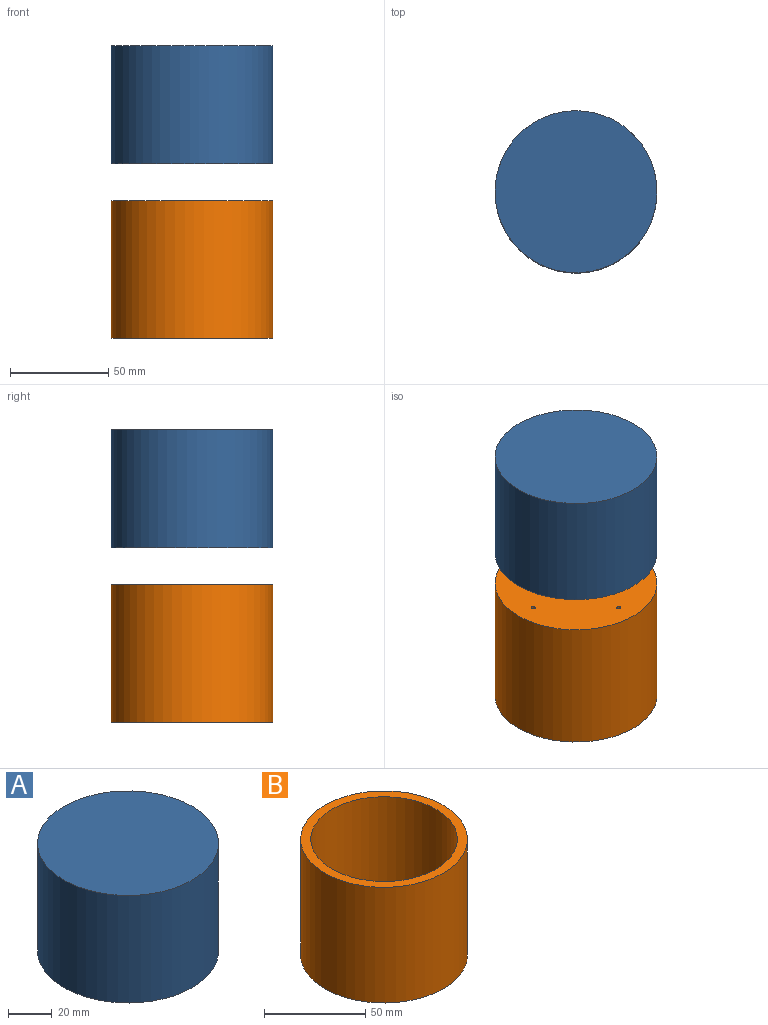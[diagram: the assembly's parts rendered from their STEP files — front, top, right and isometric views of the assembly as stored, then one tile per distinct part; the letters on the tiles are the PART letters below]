
ASSEMBLY  parts=2 mates=1
PART A: 33 faces, bbox 82.8x82.8x60.3 mm
  f0: cylinder r=36.25mm len=72.5mm, axis (0,0,1), area 11724.5mm2, adj f3,f4,f6,f8,f10,f12,f14,f17
  f1: cylinder r=41.25mm len=82.5mm, axis (0,0,-1), area 15550.9mm2, adj f2,f3
  f2: plane 82.5x82.5mm, normal (0,0,1), area 5345.6mm2, adj f1
  f3: plane 82.5x82.5mm, normal (0,0,-1), area 1614mm2, adj f0,f1,f4,f5,f6,f8,f9,f10
  f4: plane 20.26x10.26mm, normal (1,0,0), area 150.6mm2, adj f0,f3,f5,f22
  f5: plane 10.14x10.01mm, normal (0,-1,0), area 100.1mm2, adj f3,f4,f6,f7,f22
  f6: plane 20.26x10.26mm, normal (-1,0,0), area 150.6mm2, adj f0,f3,f5,f22
  f7: plane 8.5x0.35mm, normal (0,0,1), area 2mm2, adj f5,f22
  f8: plane 20.26x10.26mm, normal (0,-1,0), area 150.6mm2, adj f0,f3,f9,f23
  f9: plane 10.14x10.01mm, normal (-1,0,0), area 100.1mm2, adj f3,f8,f10,f11,f23
  f10: plane 20.26x10.26mm, normal (0,1,0), area 150.6mm2, adj f0,f3,f9,f23
  f11: plane 8.5x0.35mm, normal (0,0,1), area 2mm2, adj f9,f23
  f12: plane 20.26x10.26mm, normal (-1,0,0), area 150.6mm2, adj f0,f3,f13,f20
  f13: plane 10.14x10.01mm, normal (0,1,0), area 100.1mm2, adj f3,f12,f14,f15,f20
  f14: plane 20.26x10.26mm, normal (1,0,0), area 150.6mm2, adj f0,f3,f13,f20
  f15: plane 8.5x0.35mm, normal (0,0,1), area 2mm2, adj f13,f20
  f16: plane 10.14x10.01mm, normal (1,0,0), area 100.1mm2, adj f3,f17,f18,f19,f21
  f17: plane 20.26x10.26mm, normal (0,-1,0), area 150.6mm2, adj f0,f3,f16,f21
  f18: plane 20.26x10.26mm, normal (0,1,0), area 150.6mm2, adj f0,f3,f16,f21
  f19: plane 8.5x0.35mm, normal (0,0,1), area 2mm2, adj f16,f21
  f20: cone r=36.25mm half-angle=45deg, axis (0,0,1), area 144.3mm2, adj f0,f12,f13,f14,f15
  f21: cone r=36.25mm half-angle=45deg, axis (0,0,1), area 144.3mm2, adj f0,f16,f17,f18,f19
  f22: cone r=36.25mm half-angle=45deg, axis (0,0,1), area 144.3mm2, adj f0,f4,f5,f6,f7
  f23: cone r=36.25mm half-angle=45deg, axis (0,0,1), area 144.3mm2, adj f0,f8,f9,f10,f11
  f24: cylinder r=1mm len=8mm, axis (0,0,-1), area 50.3mm2, adj f3,f25
  f25: plane 2x2mm, normal (0,0,-1), area 3.1mm2, adj f24
  f26: cylinder r=1mm len=8mm, axis (0,0,-1), area 50.3mm2, adj f3,f27
  f27: plane 2x2mm, normal (0,0,-1), area 3.1mm2, adj f26
  f28: cylinder r=1mm len=8mm, axis (0,0,-1), area 50.3mm2, adj f3,f29
  f29: plane 2x2mm, normal (0,0,-1), area 3.1mm2, adj f28
  f30: cylinder r=1mm len=8mm, axis (0,0,-1), area 50.3mm2, adj f3,f31
  f31: plane 2x2mm, normal (0,0,-1), area 3.1mm2, adj f30
  f32: plane 72.5x72.5mm, normal (0,0,-1), area 4128.2mm2, adj f0
PART B: 10 faces, bbox 82.5x82.5x70 mm
  f0: cylinder r=41.25mm len=82.5mm, axis (0,0,-1), area 18142.7mm2, adj f1,f5
  f1: plane 82.5x82.5mm, normal (0,0,1), area 1217.4mm2, adj f0,f2
  f2: cylinder r=36.25mm len=72.5mm, axis (0,0,1), area 15488.1mm2, adj f1,f4
  f3: cylinder r=13.5mm len=27mm, axis (0,0,-1), area 169.6mm2, adj f4,f5
  f4: plane 72.5x72.5mm, normal (0,0,1), area 3543.1mm2, adj f2,f3,f6,f7,f8,f9
  f5: plane 82.5x82.5mm, normal (0,0,-1), area 4760.5mm2, adj f0,f3,f6,f7,f8,f9
  f6: cylinder r=1mm len=2mm, axis (0,0,-1), area 12.6mm2, adj f4,f5
  f7: cylinder r=1mm len=2mm, axis (0,0,-1), area 12.6mm2, adj f4,f5
  f8: cylinder r=1mm len=2mm, axis (0,0,-1), area 12.6mm2, adj f4,f5
  f9: cylinder r=1mm len=2mm, axis (0,0,-1), area 12.6mm2, adj f4,f5
PLACE A t=(-45.6,28.19,-53.24)mm fixed
PLACE B rot(axis=(0,-1,0),180deg) t=(-45.6,28.19,67.94)mm
MATE slider B.f0 <-> A.f1  axis (0,0,1) through (-45.6,28.19,2.94)mm
